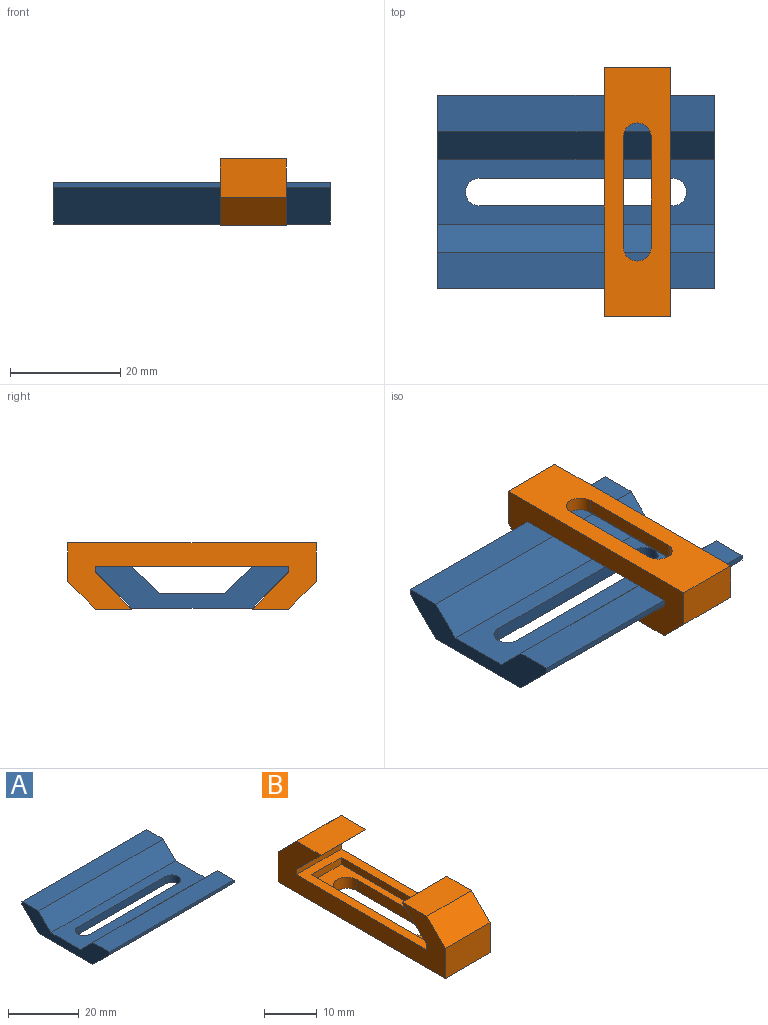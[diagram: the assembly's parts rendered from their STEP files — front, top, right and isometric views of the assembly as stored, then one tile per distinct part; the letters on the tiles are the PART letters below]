
ASSEMBLY  parts=2 mates=1
PART A: 16 faces, bbox 50x35x7.6 mm
  f0: plane 50x6.6mm, normal (0,0,1), area 330mm2, adj f1,f2,f4,f8
  f1: plane 35x7.6mm, normal (-1,0,0), area 138.4mm2, adj f0,f3,f4,f5,f6,f7,f8,f9
  f2: plane 35x7.6mm, normal (1,0,0), area 138.4mm2, adj f0,f3,f4,f5,f6,f7,f8,f9
  f3: plane 50x1mm, normal (0,1,0), area 50mm2, adj f1,f2,f5,f11
  f4: plane 50x1mm, normal (0,-1,0), area 50mm2, adj f0,f1,f2,f10
  f5: plane 50x6.6mm, normal (0,0,1), area 330mm2, adj f1,f2,f3,f9
  f6: plane 50x21.8mm, normal (0,0,-1), area 895.4mm2, adj f1,f2,f10,f11,f12,f13,f14,f15
  f7: plane 50x11.8mm, normal (0,0,1), area 395.4mm2, adj f1,f2,f8,f9,f12,f13,f14,f15
  f8: plane 50x5mm, normal (0,0.71,0.71), area 353.6mm2, adj f0,f1,f2,f7
  f9: plane 50x5mm, normal (0,-0.71,0.71), area 353.6mm2, adj f1,f2,f5,f7
  f10: plane 50x6.6mm, normal (0,-0.71,-0.71), area 466.7mm2, adj f1,f2,f4,f6
  f11: plane 50x6.6mm, normal (0,0.71,-0.71), area 466.7mm2, adj f1,f2,f3,f6
  f12: plane 35x2.6mm, normal (0,-1,0), area 91mm2, adj f6,f7,f14,f15
  f13: plane 35x2.6mm, normal (0,1,0), area 91mm2, adj f6,f7,f14,f15
  f14: cylinder r=2.5mm len=5mm, axis (0,0,1), area 20.4mm2, adj f6,f7,f12,f13
  f15: cylinder r=2.5mm len=5mm, axis (0,0,-1), area 20.4mm2, adj f6,f7,f12,f13
PART B: 23 faces, bbox 12x45x12 mm
  f0: plane 12x6.6mm, normal (0,0,1), area 79.2mm2, adj f1,f2,f11,f12
  f1: plane 45x12mm, normal (-1,0,0), area 285.6mm2, adj f0,f3,f4,f5,f6,f7,f8,f9
  f2: plane 45x12mm, normal (1,0,0), area 285.6mm2, adj f0,f3,f4,f5,f6,f7,f8,f9
  f3: plane 12x7mm, normal (0,1,0), area 84mm2, adj f1,f2,f6,f13
  f4: plane 12x7mm, normal (0,-1,0), area 84mm2, adj f1,f2,f6,f12
  f5: plane 12x6.6mm, normal (0,0,1), area 79.2mm2, adj f1,f2,f7,f13
  f6: plane 45x12mm, normal (0,0,-1), area 420.4mm2, adj f1,f2,f3,f4,f19,f20,f21,f22
  f7: plane 12x6.6mm, normal (0,-0.71,-0.71), area 112mm2, adj f1,f2,f5,f8
  f8: plane 12x1.2mm, normal (0,-1,0), area 14.4mm2, adj f1,f2,f7,f9
  f9: plane 35x12mm, normal (0,0,1), area 172mm2, adj f1,f2,f8,f10,f14,f15,f16,f17
  f10: plane 12x1.2mm, normal (0,1,0), area 14.4mm2, adj f1,f2,f9,f11
  f11: plane 12x6.6mm, normal (0,0.71,-0.71), area 112mm2, adj f0,f1,f2,f10
  f12: plane 12x5mm, normal (0,-0.71,0.71), area 84.9mm2, adj f0,f1,f2,f4
  f13: plane 12x5mm, normal (0,0.71,0.71), area 84.9mm2, adj f1,f2,f3,f5
  f14: plane 31x1.6mm, normal (-1,0,0), area 49.6mm2, adj f9,f15,f17,f18
  f15: plane 8x1.6mm, normal (0,-1,0), area 12.8mm2, adj f9,f14,f16,f18
  f16: plane 31x1.6mm, normal (1,0,0), area 49.6mm2, adj f9,f15,f17,f18
  f17: plane 8x1.6mm, normal (0,1,0), area 12.8mm2, adj f9,f14,f16,f18
  f18: plane 31x8mm, normal (0,0,1), area 128.4mm2, adj f14,f15,f16,f17,f19,f20,f21,f22
  f19: plane 20x2.6mm, normal (-1,0,0), area 52mm2, adj f6,f18,f21,f22
  f20: plane 20x2.6mm, normal (1,0,0), area 52mm2, adj f6,f18,f21,f22
  f21: cylinder r=2.5mm len=5mm, axis (0,0,1), area 20.4mm2, adj f6,f18,f19,f20
  f22: cylinder r=2.5mm len=5mm, axis (0,0,-1), area 20.4mm2, adj f6,f18,f19,f20
PLACE A t=(-17.38,-6.2,2.39)mm fixed
PLACE B rot(axis=(0,-1,0),180deg) t=(-6.28,-6.2,14.19)mm
MATE slider B.f2 <-> A.f1  axis (-1,0,0) through (-12.28,-23.7,9.99)mm
